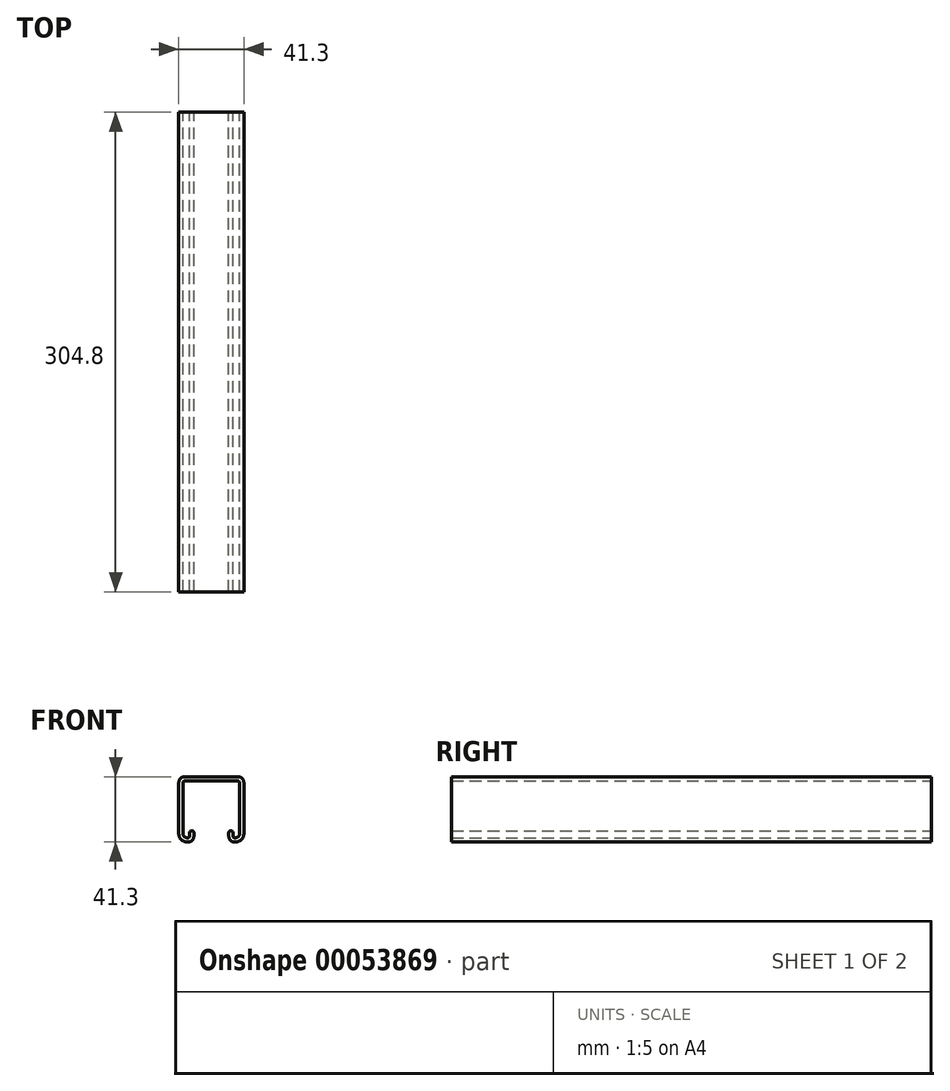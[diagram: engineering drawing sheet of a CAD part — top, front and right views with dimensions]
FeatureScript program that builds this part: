
annotation { "Feature Type Name" : "Feature", "Feature Type Description" : "" }
export const myFeature = defineFeature(function(context is Context, id is Id, definition is map)
    precondition{}
    {
        {
            var Q0;
            Q0=qCreatedBy(makeId("Front.planeOp"),FACE);
            var sketch = newSketch(context, id + "F0", { "sketchPlane" : qUnion([Q0])});
            skFitSpline(sketch, "E0.MirrorCS", {"points": [v(-253.65, -50.16) * mm, v(-253.65, -39.24) * mm, v(-253.65, -28.32) * mm, v(-253.65, -17.4) * mm]});
            skFitSpline(sketch, "E1.MirrorCS", {"points": [v(-256.35, -17.4) * mm, v(-256.35, -28.32) * mm, v(-256.35, -39.24) * mm, v(-256.35, -50.16) * mm]});
            skArc(sketch, "E2.MirrorCS", {"start": v(-253.65, -17.4) * mm, "mid": v(-254.67, -14.94) * mm, "end": v(-257.13, -13.92) * mm});
            skArc(sketch, "E3.MirrorCS", {"start": v(-257.13, -16.61) * mm, "mid": v(-256.58, -16.84) * mm, "end": v(-256.35, -17.4) * mm});
            skFitSpline(sketch, "E4.MirrorCS", {"points": [v(-257.13, -13.92) * mm, v(-268.58, -13.92) * mm, v(-280.03, -13.92) * mm, v(-291.48, -13.92) * mm]});
            skFitSpline(sketch, "E5.MirrorCS", {"points": [v(-291.48, -16.61) * mm, v(-280.03, -16.61) * mm, v(-268.58, -16.61) * mm, v(-257.13, -16.61) * mm]});
            skArc(sketch, "E6.MirrorCS", {"start": v(-291.48, -13.92) * mm, "mid": v(-293.94, -14.94) * mm, "end": v(-294.95, -17.4) * mm});
            skFitSpline(sketch, "E7.MirrorCS", {"points": [v(-294.95, -17.4) * mm, v(-294.95, -28.32) * mm, v(-294.95, -39.24) * mm, v(-294.95, -50.16) * mm]});
            skArc(sketch, "E8.MirrorCS", {"start": v(-292.26, -17.4) * mm, "mid": v(-292.03, -16.84) * mm, "end": v(-291.48, -16.61) * mm});
            skFitSpline(sketch, "E9.MirrorCS", {"points": [v(-292.26, -17.4) * mm, v(-292.26, -28.32) * mm, v(-292.26, -39.24) * mm, v(-292.26, -50.16) * mm]});
            skArc(sketch, "E10.MirrorCS", {"start": v(-289.9, -52.53) * mm, "mid": v(-291.57, -51.84) * mm, "end": v(-292.26, -50.16) * mm});
            skArc(sketch, "E11.MirrorCS", {"start": v(-294.95, -50.16) * mm, "mid": v(-293.47, -53.74) * mm, "end": v(-289.9, -55.22) * mm});
            skFitSpline(sketch, "E12.MirrorCS", {"points": [v(-289.9, -55.22) * mm, v(-289.56, -55.22) * mm, v(-289.22, -55.22) * mm, v(-288.88, -55.22) * mm]});
            skFitSpline(sketch, "E13.MirrorCS", {"points": [v(-288.88, -52.53) * mm, v(-289.22, -52.53) * mm, v(-289.56, -52.53) * mm, v(-289.9, -52.53) * mm]});
            skArc(sketch, "E14.MirrorCS", {"start": v(-288.1, -51.75) * mm, "mid": v(-288.33, -52.3) * mm, "end": v(-288.88, -52.53) * mm});
            skFitSpline(sketch, "E15.MirrorCS", {"points": [v(-288.1, -49.4) * mm, v(-288.1, -50.19) * mm, v(-288.1, -50.97) * mm, v(-288.1, -51.75) * mm]});
            skArc(sketch, "E16.MirrorCS", {"start": v(-285.4, -49.4) * mm, "mid": v(-286.75, -48.06) * mm, "end": v(-288.1, -49.4) * mm});
            skFitSpline(sketch, "E17.MirrorCS", {"points": [v(-285.4, -51.75) * mm, v(-285.4, -50.97) * mm, v(-285.4, -50.19) * mm, v(-285.4, -49.4) * mm]});
            skArc(sketch, "E18.MirrorCS", {"start": v(-288.88, -55.22) * mm, "mid": v(-286.42, -54.2) * mm, "end": v(-285.4, -51.75) * mm});
            skFitSpline(sketch, "E19.MirrorCS", {"points": [v(-263.2, -49.4) * mm, v(-263.2, -50.19) * mm, v(-263.2, -50.97) * mm, v(-263.2, -51.75) * mm]});
            skArc(sketch, "E20.MirrorCS", {"start": v(-260.51, -49.4) * mm, "mid": v(-261.86, -48.06) * mm, "end": v(-263.2, -49.4) * mm});
            skFitSpline(sketch, "E21.MirrorCS", {"points": [v(-260.51, -51.75) * mm, v(-260.51, -50.97) * mm, v(-260.51, -50.19) * mm, v(-260.51, -49.4) * mm]});
            skArc(sketch, "E22.MirrorCS", {"start": v(-263.2, -51.75) * mm, "mid": v(-262.19, -54.2) * mm, "end": v(-259.73, -55.22) * mm});
            skArc(sketch, "E23.MirrorCS", {"start": v(-259.73, -52.53) * mm, "mid": v(-260.28, -52.3) * mm, "end": v(-260.51, -51.75) * mm});
            skFitSpline(sketch, "E24.MirrorCS", {"points": [v(-258.72, -52.53) * mm, v(-259.05, -52.53) * mm, v(-259.4, -52.53) * mm, v(-259.73, -52.53) * mm]});
            skFitSpline(sketch, "E25.MirrorCS", {"points": [v(-259.73, -55.22) * mm, v(-259.4, -55.22) * mm, v(-259.05, -55.22) * mm, v(-258.72, -55.22) * mm]});
            skArc(sketch, "E26.MirrorCS", {"start": v(-258.72, -55.22) * mm, "mid": v(-255.14, -53.74) * mm, "end": v(-253.65, -50.16) * mm});
            skArc(sketch, "E27.MirrorCS", {"start": v(-256.35, -50.16) * mm, "mid": v(-257.04, -51.84) * mm, "end": v(-258.72, -52.53) * mm});
            skSolve(sketch);
        }
        {
            var Q0;
            Q0=makeQuery(id+"F0.imprint","IMPRINT",FACE,{"disambiguationData":[TD([[makeQuery(id+"F0.imprint","IMPRINT",EDGE,{"derivedFrom":sQuery(id+"F0.wireOp",EDGE,"E0.MirrorCS")}),1.0]])]});
            extrude(context, id + "F1", {"entities" : qUnion([Q0]), "depth" : 304.8 * mm});
        }
    });
